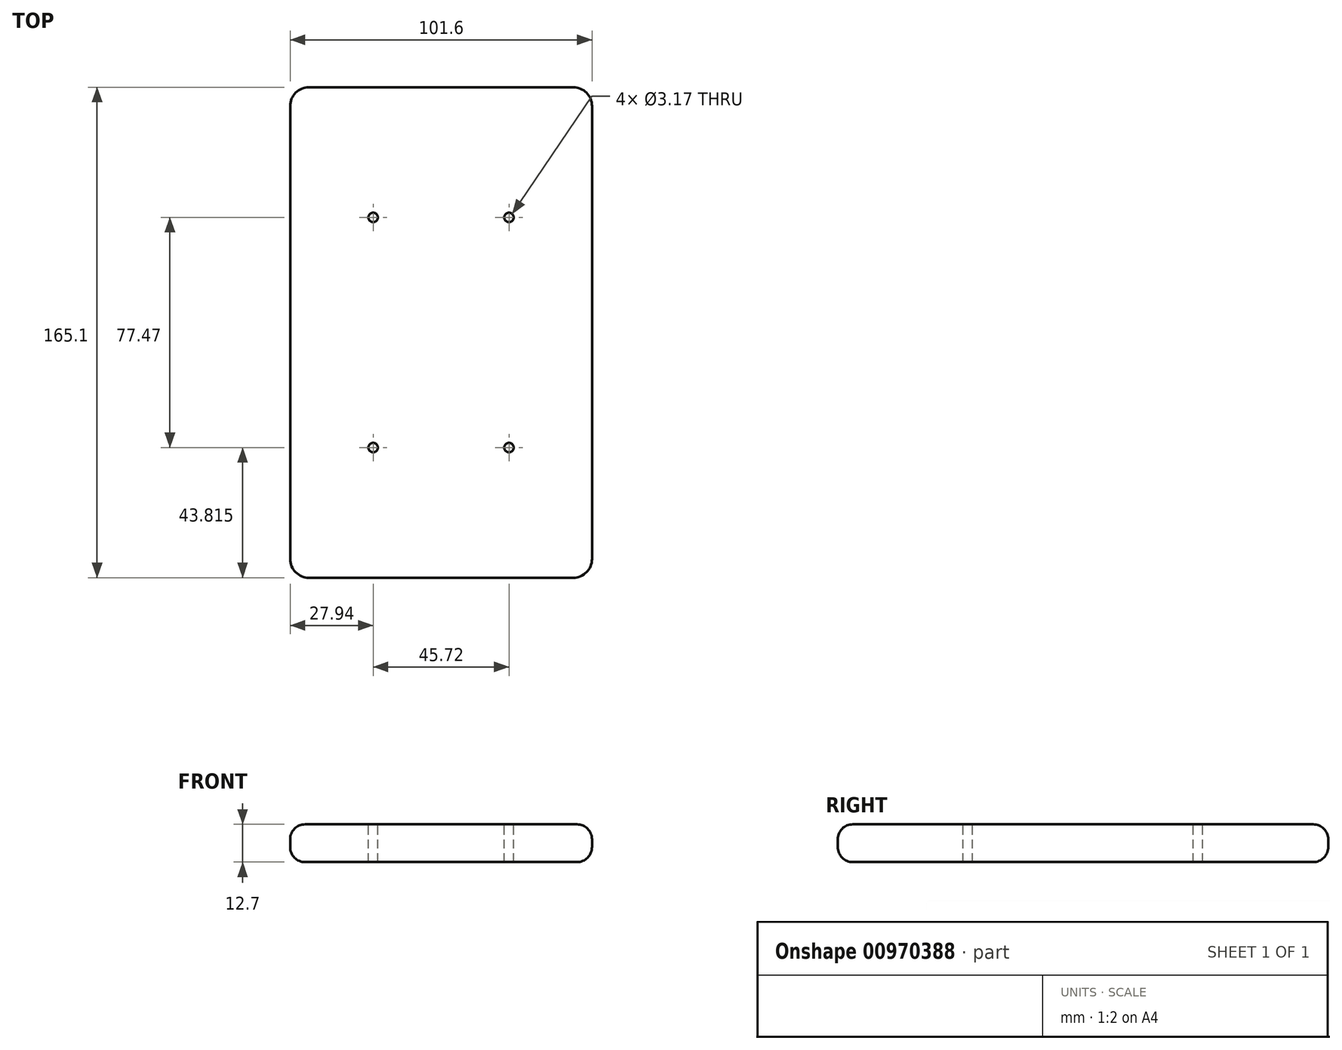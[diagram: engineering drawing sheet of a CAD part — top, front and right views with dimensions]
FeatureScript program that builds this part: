
annotation { "Feature Type Name" : "Feature", "Feature Type Description" : "" }
export const myFeature = defineFeature(function(context is Context, id is Id, definition is map)
    precondition{}
    {
        {
            var Q0;
            Q0=qCreatedBy(makeId("Top.planeOp"),FACE);
            var sketch = newSketch(context, id + "F0", { "sketchPlane" : qUnion([Q0])});
            skLineSegment(sketch, "E0.bottom", {"start": v(44.45, 82.55) * mm, "end": v(-44.45, 82.55) * mm});
            skLineSegment(sketch, "E0.top", {"start": v(44.45, -82.55) * mm, "end": v(-44.45, -82.55) * mm});
            skLineSegment(sketch, "E0.left", {"start": v(50.8, 76.2) * mm, "end": v(50.8, -76.2) * mm});
            skLineSegment(sketch, "E0.right", {"start": v(-50.8, 76.2) * mm, "end": v(-50.8, -76.2) * mm});
            skPoint(sketch, "E0.middle", {"position": v(0, 0) * mm});
            skPoint(sketch, "E1.visualSharp", {"position": v(-50.8, 82.55) * mm});
            skArc(sketch, "E1.filletArc", {"start": v(-44.45, 82.55) * mm, "mid": v(-48.94, 80.7) * mm, "end": v(-50.8, 76.2) * mm});
            skPoint(sketch, "E2.visualSharp", {"position": v(50.8, 82.55) * mm});
            skArc(sketch, "E2.filletArc", {"start": v(50.8, 76.2) * mm, "mid": v(48.94, 80.7) * mm, "end": v(44.45, 82.55) * mm});
            skPoint(sketch, "E3.visualSharp", {"position": v(50.8, -82.55) * mm});
            skArc(sketch, "E3.filletArc", {"start": v(44.45, -82.55) * mm, "mid": v(48.94, -80.7) * mm, "end": v(50.8, -76.2) * mm});
            skPoint(sketch, "E4.visualSharp", {"position": v(-50.8, -82.55) * mm});
            skArc(sketch, "E4.filletArc", {"start": v(-50.8, -76.2) * mm, "mid": v(-48.94, -80.7) * mm, "end": v(-44.45, -82.55) * mm});
            skSolve(sketch);
        }
        {
            var Q0;
            Q0 = qSketchRegion(id + "F0", true);
            extrude(context, id + "F1", {"entities" : qUnion([Q0]), "depth" : 12.7 * mm, "offsetDistance" : 25.4 * mm});
        }
        {
            var Q0;
            Q0=makeQuery(id+"F1.opExtrude","CAP_FACE",FACE,{"disambiguationData":[OSD([sQuery(id+"F0.wireOp",EDGE,"E0.bottom"),sQuery(id+"F0.wireOp",EDGE,"E0.top"),sQuery(id+"F0.wireOp",EDGE,"E0.left"),sQuery(id+"F0.wireOp",EDGE,"E0.right"),sQuery(id+"F0.wireOp",EDGE,"E1.filletArc"),sQuery(id+"F0.wireOp",EDGE,"E2.filletArc"),sQuery(id+"F0.wireOp",EDGE,"E3.filletArc"),sQuery(id+"F0.wireOp",EDGE,"E4.filletArc")])],"isStart":false});
            var Q1;
            Q1=makeQuery(id+"F1.opExtrude","CAP_FACE",FACE,{"disambiguationData":[OSD([sQuery(id+"F0.wireOp",EDGE,"E0.bottom"),sQuery(id+"F0.wireOp",EDGE,"E0.top"),sQuery(id+"F0.wireOp",EDGE,"E0.left"),sQuery(id+"F0.wireOp",EDGE,"E0.right"),sQuery(id+"F0.wireOp",EDGE,"E1.filletArc"),sQuery(id+"F0.wireOp",EDGE,"E2.filletArc"),sQuery(id+"F0.wireOp",EDGE,"E3.filletArc"),sQuery(id+"F0.wireOp",EDGE,"E4.filletArc")])],"isStart":true});
            fillet(context, id + "F2", {"entities" : qUnion([Q0, Q1]), "radius" : 5.08 * mm, "tangentPropagation" : true, "allowEdgeOverflow" : false});
        }
        {
            var Q0;
            Q0=makeQuery(id+"F1.opExtrude","CAP_FACE",FACE,{"disambiguationData":[OSD([sQuery(id+"F0.wireOp",EDGE,"E0.bottom"),sQuery(id+"F0.wireOp",EDGE,"E0.top"),sQuery(id+"F0.wireOp",EDGE,"E0.left"),sQuery(id+"F0.wireOp",EDGE,"E0.right"),sQuery(id+"F0.wireOp",EDGE,"E1.filletArc"),sQuery(id+"F0.wireOp",EDGE,"E2.filletArc"),sQuery(id+"F0.wireOp",EDGE,"E3.filletArc"),sQuery(id+"F0.wireOp",EDGE,"E4.filletArc")])],"isStart":false});
            var sketch = newSketch(context, id + "F3", { "sketchPlane" : qUnion([Q0])});
            skCircle(sketch, "E5", {"center": v(-22.86, 38.74) * mm, "radius": 1.59 * mm});
            skLineSegment(sketch, "E6", {"start": v(0, 0) * mm, "end": v(0, 77.47) * mm, "construction": true});
            skLineSegment(sketch, "E7", {"start": v(-45.72, 38.74) * mm, "end": v(0, 38.74) * mm, "construction": true});
            skCircle(sketch, "E8.MirrorC", {"center": v(22.86, 38.74) * mm, "radius": 1.59 * mm});
            skLineSegment(sketch, "E9", {"start": v(0, 0) * mm, "end": v(45.72, 0) * mm, "construction": true});
            skCircle(sketch, "E10.MirrorC", {"center": v(-22.86, -38.74) * mm, "radius": 1.59 * mm});
            skCircle(sketch, "E11.MirrorC", {"center": v(22.86, -38.73) * mm, "radius": 1.59 * mm});
            skSolve(sketch);
        }
        {
            var Q0;
            Q0 = qSketchRegion(id + "F3", true);
            extrude(context, id + "F4", {"entities" : qUnion([Q0]), "operationType" : NewBodyOperationType.REMOVE, "endBound" : BoundingType.THROUGH_ALL, "oppositeDirection" : true, "depth" : 109.47 * mm, "offsetDistance" : 25.4 * mm});
        }
    });
